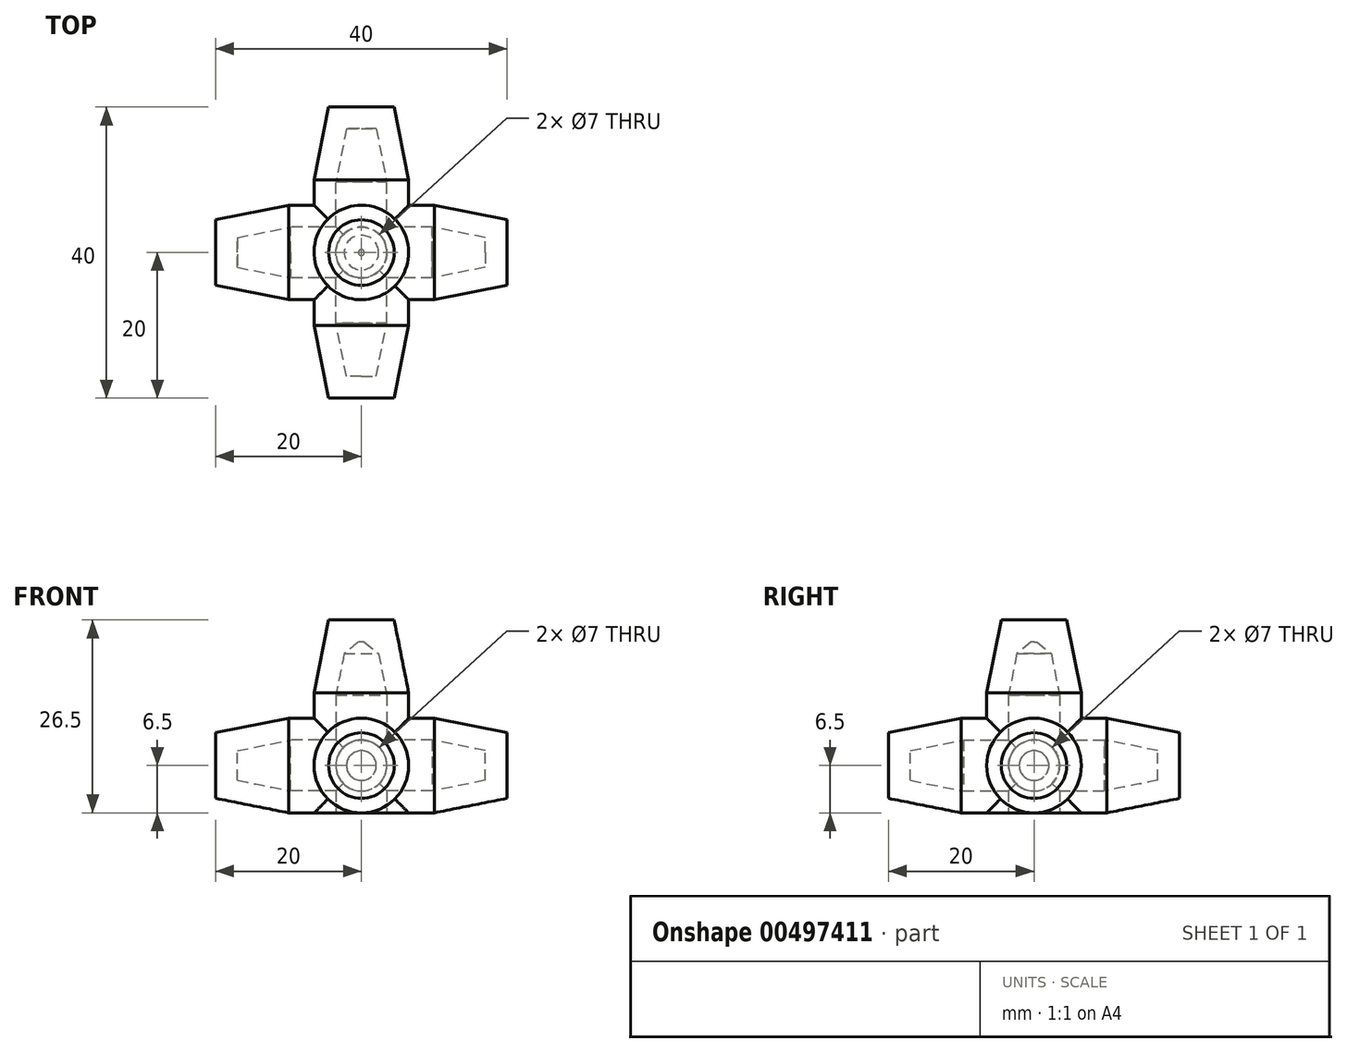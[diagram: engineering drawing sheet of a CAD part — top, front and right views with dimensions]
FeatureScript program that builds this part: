
annotation { "Feature Type Name" : "Feature", "Feature Type Description" : "" }
export const myFeature = defineFeature(function(context is Context, id is Id, definition is map)
    precondition{}
    {
        {
            var Q0;
            Q0=qCreatedBy(makeId("Top.planeOp"),FACE);
            var sketch = newSketch(context, id + "F0", { "sketchPlane" : qUnion([Q0])});
            skCircle(sketch, "E0", {"center": v(0, 0) * mm, "radius": 6.5 * mm});
            skSolve(sketch);
        }
        {
            var Q0;
            Q0=makeQuery(id+"F0.imprint","IMPRINT",FACE,{"disambiguationData":[TD([[makeQuery(id+"F0.imprint","IMPRINT",EDGE,{"derivedFrom":sQuery(id+"F0.wireOp",EDGE,"E0")}),1.0]])]});
            extrude(context, id + "F1", {"entities" : qUnion([Q0]), "depth" : 26.5 * mm, "offsetDistance" : 25.4 * mm});
        }
        {
            var Q0;
            Q0=qCreatedBy(makeId("Right.planeOp"),FACE);
            var sketch = newSketch(context, id + "F2", { "sketchPlane" : qUnion([Q0])});
            skCircle(sketch, "E1", {"center": v(0, 6.5) * mm, "radius": 6.5 * mm});
            skLineSegment(sketch, "E2.0", {"start": v(-6.5, 0) * mm, "end": v(6.5, 0) * mm});
            skLineSegment(sketch, "E3", {"start": v(6.5, 25.4) * mm, "end": v(6.5, 0) * mm});
            skSolve(sketch);
        }
        {
            var Q0;
            {var subQ0=sQuery(id+"F2.wireOp",EDGE,"E1");var subQ1=makeQuery(id+"F2.imprint","INTERSECT",VERTEX,{"derivedFrom":[subQ0,sQuery(id+"F2.wireOp",EDGE,"E2.0")]});Q0=makeQuery(id+"F2.imprint","IMPRINT",FACE,{"disambiguationData":[TD([[makeQuery(id+"F2.imprint","IMPRINT",EDGE,{"disambiguationData":[TD([[subQ1,1.0]])],"derivedFrom":subQ0}),1.0]])]});}
            extrude(context, id + "F3", {"entities" : qUnion([Q0]), "operationType" : NewBodyOperationType.ADD, "endBound" : BoundingType.SYMMETRIC, "depth" : 40 * mm, "offsetDistance" : 25.4 * mm});
        }
        {
            var Q0;
            Q0=qCreatedBy(makeId("Front.planeOp"),FACE);
            var sketch = newSketch(context, id + "F4", { "sketchPlane" : qUnion([Q0])});
            skCircle(sketch, "E4", {"center": v(0, 6.5) * mm, "radius": 6.5 * mm});
            skSolve(sketch);
        }
        {
            var Q0;
            Q0 = qSketchRegion(id + "F4", true);
            extrude(context, id + "F5", {"entities" : qUnion([Q0]), "operationType" : NewBodyOperationType.ADD, "endBound" : BoundingType.SYMMETRIC, "depth" : 40 * mm, "offsetDistance" : 25.4 * mm});
        }
        {
            var Q0;
            Q0=makeQuery(id+"F1.opExtrude","CAP_EDGE",EDGE,{"disambiguationData":[OSD([sQuery(id+"F0.wireOp",EDGE,"E0")])],"isStart":false});
            var Q1;
            Q1=makeQuery(id+"F3.opExtrude","CAP_EDGE",EDGE,{"disambiguationData":[OSD([sQuery(id+"F2.wireOp",EDGE,"E1")])],"isStart":false});
            var Q2;
            Q2=makeQuery(id+"F5.opExtrude","CAP_EDGE",EDGE,{"disambiguationData":[OSD([sQuery(id+"F4.wireOp",EDGE,"E4")])],"isStart":false});
            chamfer(context, id + "F6", {"entities" : qUnion([Q0, Q1, Q2]), "chamferType" : ChamferType.TWO_OFFSETS, "width1" : 2 * mm, "oppositeDirection" : false, "width2" : 10 * mm, "tangentPropagation" : true});
        }
        {
            var Q0;
            Q0=makeQuery(id+"F5.opExtrude","CAP_EDGE",EDGE,{"disambiguationData":[OSD([sQuery(id+"F4.wireOp",EDGE,"E4")])],"isStart":true});
            var Q1;
            Q1=makeQuery(id+"F3.opExtrude","CAP_EDGE",EDGE,{"disambiguationData":[OSD([sQuery(id+"F2.wireOp",EDGE,"E1")])],"isStart":true});
            chamfer(context, id + "F7", {"entities" : qUnion([Q0, Q1]), "chamferType" : ChamferType.TWO_OFFSETS, "width1" : 2 * mm, "oppositeDirection" : true, "width2" : 10 * mm, "tangentPropagation" : true});
        }
        {
            var Q0;
            Q0=makeQuery(id+"F1.opExtrude","CAP_FACE",FACE,{"disambiguationData":[OSD([sQuery(id+"F0.wireOp",EDGE,"E0")])],"isStart":true});
            shell(context, id + "F8", {"entities" : qUnion([Q0]), "thickness" : 3 * mm});
        }
        {
            var Q0;
            {var subQ0=sQuery(id+"F0.wireOp",EDGE,"E0");Q0=makeQuery(id+"F8.opShell","OFFSET_EDGE",EDGE,{"disambiguationData":[OSD([subQ0]),TDD([makeQuery(id+"F6.opChamfer","BLEND_EDGE",EDGE,{"blendedFrom":[makeQuery(id+"F1.opExtrude","CAP_EDGE",EDGE,{"disambiguationData":[OSD([subQ0])],"isStart":false}),makeQuery(id+"F1.opExtrude","CAP_FACE",FACE,{"disambiguationData":[OSD([subQ0])],"isStart":false})],"blendedInto":[makeQuery(id+"F1.opExtrude","CAP_FACE",FACE,{"disambiguationData":[OSD([subQ0])],"isStart":false})]})])]});}
            chamfer(context, id + "F9", {"entities" : qUnion([Q0]), "width" : 2 * mm, "tangentPropagation" : true});
        }
    });
